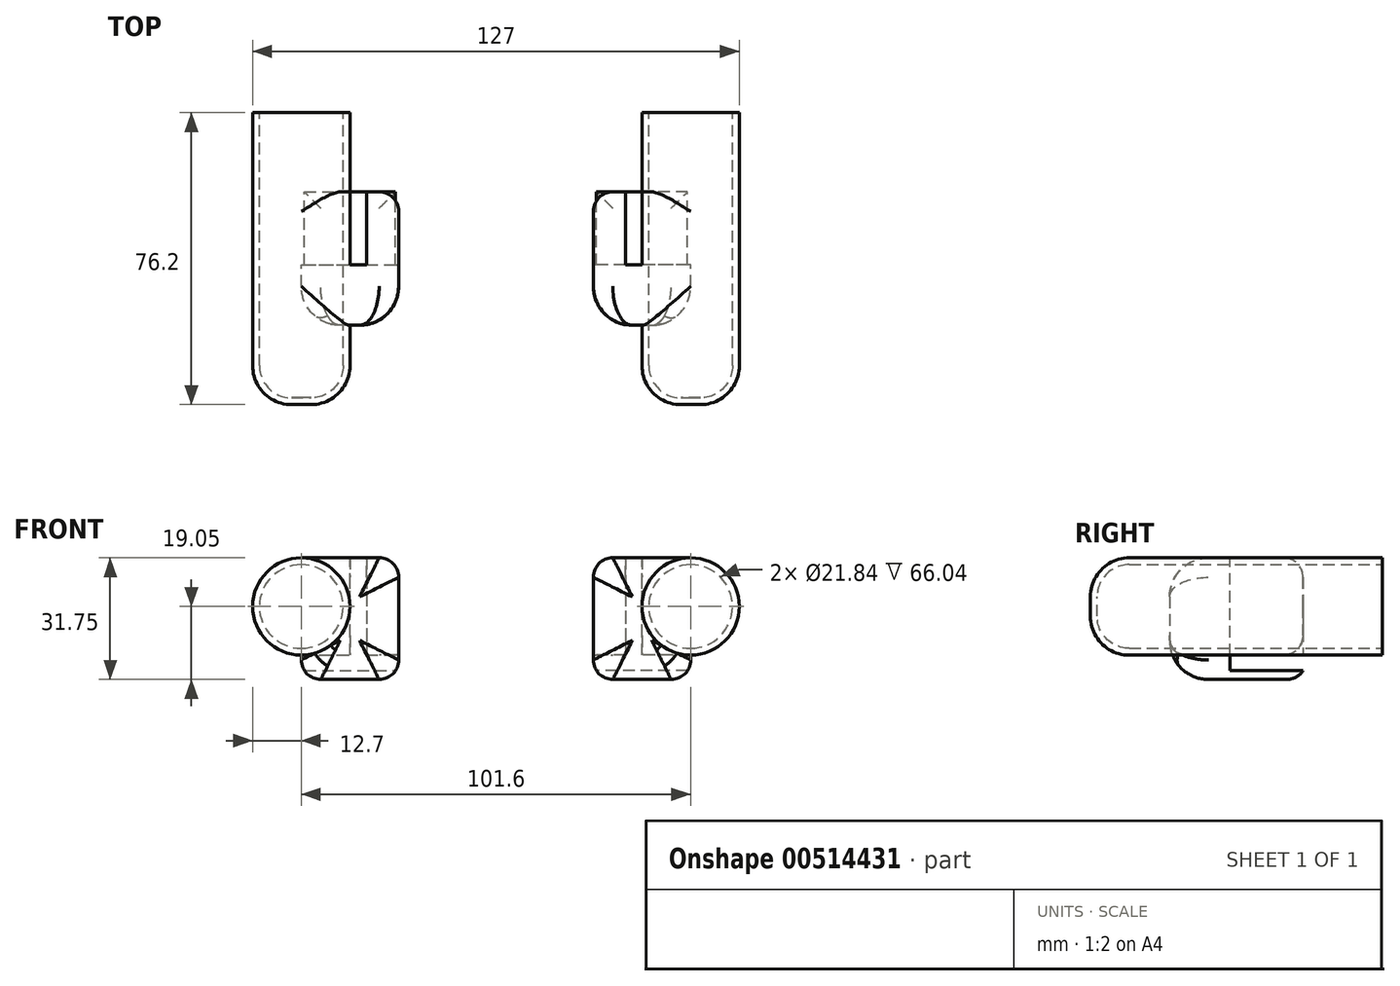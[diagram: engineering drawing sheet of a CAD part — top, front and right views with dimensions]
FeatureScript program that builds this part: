
annotation { "Feature Type Name" : "Feature", "Feature Type Description" : "" }
export const myFeature = defineFeature(function(context is Context, id is Id, definition is map)
    precondition{}
    {
        {
            var Q0;
            Q0=qCreatedBy(makeId("Front.planeOp"),FACE);
            var sketch = newSketch(context, id + "F0", { "sketchPlane" : qUnion([Q0])});
            skCircle(sketch, "E0", {"center": v(0, 0) * mm, "radius": 12.7 * mm});
            skSolve(sketch);
        }
        {
            var Q0;
            Q0 = qSketchRegion(id + "F0", true);
            extrude(context, id + "F1", {"entities" : qUnion([Q0]), "endBound" : BoundingType.SYMMETRIC, "depth" : 76.2 * mm});
        }
        {
            var Q0;
            Q0=makeQuery(id+"F1.opExtrude","CAP_EDGE",EDGE,{"disambiguationData":[OSD([sQuery(id+"F0.wireOp",EDGE,"E0")])],"isStart":false});
            fillet(context, id + "F2", {"entities" : qUnion([Q0]), "radius" : 10.16 * mm, "tangentPropagation" : true, "allowEdgeOverflow" : false});
        }
        {
            var Q0;
            Q0=makeQuery(id+"F1.opExtrude","CAP_FACE",FACE,{"disambiguationData":[OSD([sQuery(id+"F0.wireOp",EDGE,"E0")])],"isStart":true});
            shell(context, id + "F3", {"entities" : qUnion([Q0]), "thickness" : 1.78 * mm});
        }
        {
            var Q0;
            Q0=qCreatedBy(makeId("Front.planeOp"),FACE);
            var sketch = newSketch(context, id + "F4", { "sketchPlane" : qUnion([Q0])});
            skArc(sketch, "E1.0", {"start": v(0, 12.7) * mm, "mid": v(-12.7, 0) * mm, "end": v(0, -12.7) * mm});
            skLineSegment(sketch, "E2", {"start": v(0, 12.7) * mm, "end": v(-25.4, 12.7) * mm});
            skLineSegment(sketch, "E3", {"start": v(-25.4, 12.7) * mm, "end": v(-25.4, -19.05) * mm});
            skLineSegment(sketch, "E4", {"start": v(-25.4, -19.05) * mm, "end": v(0, -19.05) * mm});
            skLineSegment(sketch, "E5", {"start": v(0, -19.05) * mm, "end": v(0, -12.7) * mm});
            skSolve(sketch);
        }
        {
            var Q0;
            Q0 = qSketchRegion(id + "F4", true);
            extrude(context, id + "F5", {"entities" : qUnion([Q0]), "operationType" : NewBodyOperationType.ADD, "endBound" : BoundingType.SYMMETRIC, "depth" : 34.8 * mm});
        }
        {
            var Q0;
            Q0=makeQuery(id+"F5.opExtrude","CAP_FACE",FACE,{"disambiguationData":[OSD([sQuery(id+"F4.wireOp",EDGE,"E1.0"),sQuery(id+"F4.wireOp",EDGE,"E2"),sQuery(id+"F4.wireOp",EDGE,"E3"),sQuery(id+"F4.wireOp",EDGE,"E4"),sQuery(id+"F4.wireOp",EDGE,"E5")])],"isStart":true});
            var sketch = newSketch(context, id + "F6", { "sketchPlane" : qUnion([Q0])});
            skLineSegment(sketch, "E6", {"start": v(12.7, 0) * mm, "end": v(12.7, 12.7) * mm});
            skLineSegment(sketch, "E7", {"start": v(12.7, 0) * mm, "end": v(12.7, -12.7) * mm});
            skLineSegment(sketch, "E8", {"start": v(0, -12.7) * mm, "end": v(12.7, -12.7) * mm});
            skLineSegment(sketch, "E9", {"start": v(0, -16.76) * mm, "end": v(17.02, -16.76) * mm});
            skLineSegment(sketch, "E10", {"start": v(17.02, 12.7) * mm, "end": v(17.02, -12.7) * mm});
            skLineSegment(sketch, "E11", {"start": v(0, -12.7) * mm, "end": v(0, -16.76) * mm});
            skLineSegment(sketch, "E12", {"start": v(12.7, 12.7) * mm, "end": v(17.02, 12.7) * mm});
            skLineSegment(sketch, "E13", {"start": v(17.02, -12.7) * mm, "end": v(25.4, -12.7) * mm});
            skLineSegment(sketch, "E14", {"start": v(25.4, -12.7) * mm, "end": v(25.4, -16.76) * mm});
            skLineSegment(sketch, "E15", {"start": v(25.4, -16.76) * mm, "end": v(17.02, -16.76) * mm});
            skSolve(sketch);
        }
        {
            var Q0;
            Q0 = qSketchRegion(id + "F6", true);
            extrude(context, id + "F7", {"entities" : qUnion([Q0]), "operationType" : NewBodyOperationType.REMOVE, "oppositeDirection" : true, "depth" : 19.05 * mm});
        }
        {
            var Q0;
            Q0=makeQuery(id+"F5.opExtrude","CAP_EDGE",EDGE,{"disambiguationData":[OSD([sQuery(id+"F4.wireOp",EDGE,"E2")])],"isStart":false});
            var Q1;
            Q1=makeQuery(id+"F5.opExtrude","CAP_EDGE",EDGE,{"disambiguationData":[OSD([sQuery(id+"F4.wireOp",EDGE,"E3")])],"isStart":false});
            var Q2;
            Q2=makeQuery(id+"F5.opExtrude","CAP_EDGE",EDGE,{"disambiguationData":[OSD([sQuery(id+"F4.wireOp",EDGE,"E4")])],"isStart":false});
            var Q3;
            Q3=makeQuery(id+"F5.opExtrude","CAP_EDGE",EDGE,{"disambiguationData":[OSD([sQuery(id+"F4.wireOp",EDGE,"E5")])],"isStart":false});
            fillet(context, id + "F8", {"entities" : qUnion([Q0, Q1, Q2, Q3]), "radius" : 10.16 * mm, "tangentPropagation" : true, "allowEdgeOverflow" : false});
        }
        {
            var Q0;
            {var subQ0=sQuery(id+"F4.wireOp",EDGE,"E3");var subQ1=sQuery(id+"F4.wireOp",EDGE,"E2");Q0=makeQuery(id+"F7.boolean.opBoolean","SPLIT",EDGE,{"disambiguationData":[TD([makeQuery(id+"F5.opExtrude","SWEPT_FACE",FACE,{"disambiguationData":[OSD([subQ1])]})])],"derivedFrom":makeQuery(id+"F5.opExtrude","CAP_EDGE",EDGE,{"disambiguationData":[OSD([subQ0])],"isStart":true})});}
            var Q1;
            {var subQ0=sQuery(id+"F4.wireOp",EDGE,"E3");var subQ1=sQuery(id+"F4.wireOp",EDGE,"E2");Q1=makeQuery(id+"F7.boolean.opBoolean","SPLIT",EDGE,{"disambiguationData":[TD([makeQuery(id+"F5.opExtrude","SWEPT_FACE",FACE,{"disambiguationData":[OSD([subQ0])]})])],"derivedFrom":makeQuery(id+"F5.opExtrude","CAP_EDGE",EDGE,{"disambiguationData":[OSD([subQ1])],"isStart":true})});}
            var Q2;
            {var subQ0=sQuery(id+"F4.wireOp",EDGE,"E2");Q2=makeQuery(id+"F7.boolean.opBoolean","SPLIT",EDGE,{"disambiguationData":[TD([makeQuery(id+"F1.opExtrude","SWEPT_FACE",FACE,{"disambiguationData":[OSD([sQuery(id+"F0.wireOp",EDGE,"E0")])]})])],"derivedFrom":makeQuery(id+"F5.opExtrude","CAP_EDGE",EDGE,{"disambiguationData":[OSD([subQ0])],"isStart":true})});}
            var Q3;
            Q3=makeQuery(id+"F7.boolean.opBoolean","COPY",EDGE,{"derivedFrom":makeQuery(id+"F7.opExtrude","CAP_EDGE",EDGE,{"disambiguationData":[OSD([sQuery(id+"F6.wireOp",EDGE,"E8")])],"isStart":true})});
            var Q4;
            Q4=makeQuery(id+"F7.boolean.opBoolean","COPY",EDGE,{"derivedFrom":makeQuery(id+"F7.opExtrude","CAP_EDGE",EDGE,{"disambiguationData":[OSD([sQuery(id+"F6.wireOp",EDGE,"E13")])],"isStart":true})});
            var Q5;
            Q5=makeQuery(id+"F5.opExtrude","CAP_EDGE",EDGE,{"disambiguationData":[OSD([sQuery(id+"F4.wireOp",EDGE,"E4")])],"isStart":true});
            var Q6;
            Q6=makeQuery(id+"F5.opExtrude","SWEPT_EDGE",EDGE,{"disambiguationData":[OSD([sQuery(id+"F4.wireOp",EDGE,"E2"),sQuery(id+"F4.wireOp",EDGE,"E3")])]});
            var Q7;
            Q7=makeQuery(id+"F5.opExtrude","SWEPT_EDGE",EDGE,{"disambiguationData":[OSD([sQuery(id+"F4.wireOp",EDGE,"E3"),sQuery(id+"F4.wireOp",EDGE,"E4")])]});
            var Q8;
            Q8=makeQuery(id+"F5.opExtrude","SWEPT_EDGE",EDGE,{"disambiguationData":[OSD([sQuery(id+"F4.wireOp",EDGE,"E4"),sQuery(id+"F4.wireOp",EDGE,"E5")])]});
            fillet(context, id + "F9", {"entities" : qUnion([Q0, Q1, Q2, Q3, Q4, Q5, Q6, Q7, Q8]), "radius" : 5.08 * mm, "tangentPropagation" : true, "allowEdgeOverflow" : false});
        }
        {
            var Q0;
            Q0=makeQuery(id+"F5.opExtrude","SWEPT_FACE",FACE,{"disambiguationData":[OSD([sQuery(id+"F4.wireOp",EDGE,"E3")])]});
            cPlane(context, id + "F10", {"entities" : qUnion([Q0]), "cplaneType" : CPlaneType.OFFSET, "offset" : 25.4 * mm, "width" : 152.4 * mm, "height" : 152.4 * mm});
        }
        {
            var Q0;
            Q0=makeQuery(id+"F1.opExtrude","SWEPT_BODY",BODY,{"disambiguationData":[OSD([sQuery(id+"F0.wireOp",EDGE,"E0")])]});
            var Q1;
            Q1=qCreatedBy(id+"F10.planeOp",FACE);
            mirror(context, id + "F11", {"entities" : qUnion([Q0]), "mirrorPlane" : qUnion([Q1])});
        }
    });
